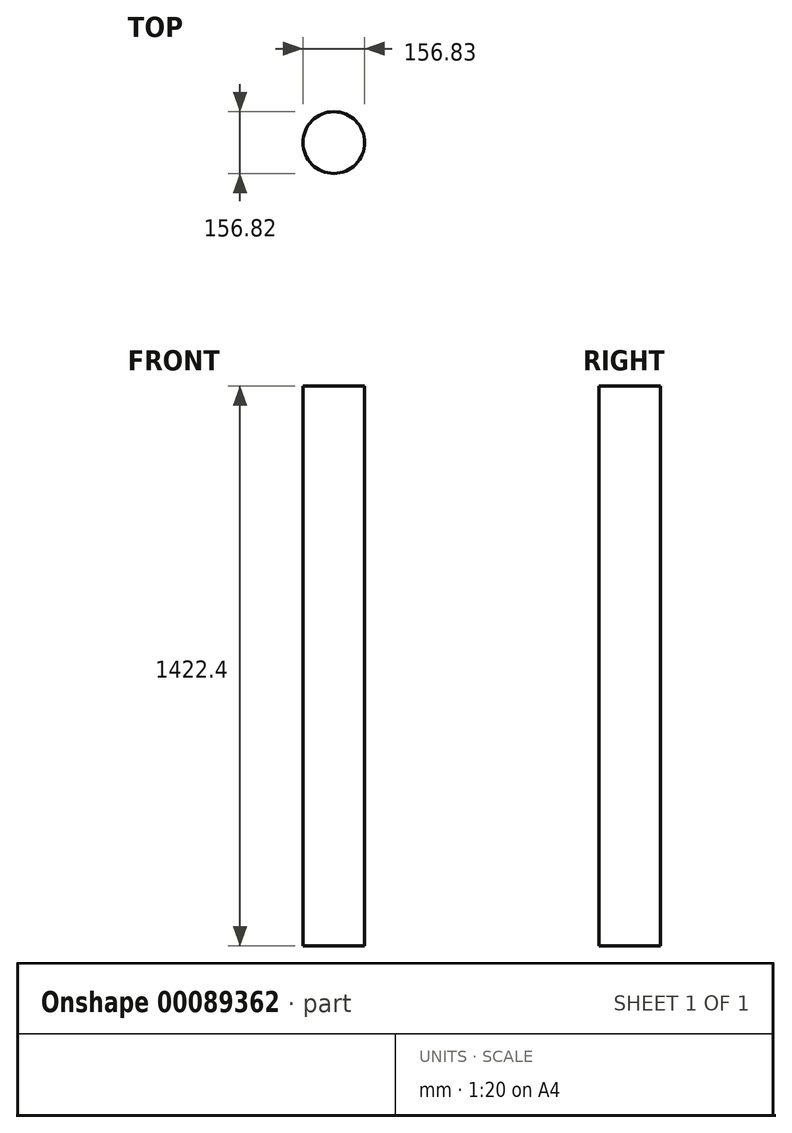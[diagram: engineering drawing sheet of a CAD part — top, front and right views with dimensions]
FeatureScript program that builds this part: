
annotation { "Feature Type Name" : "Feature", "Feature Type Description" : "" }
export const myFeature = defineFeature(function(context is Context, id is Id, definition is map)
    precondition{}
    {
        {
            var Q0;
            Q0=qCreatedBy(makeId("Top.planeOp"),FACE);
            var sketch = newSketch(context, id + "F0", { "sketchPlane" : qUnion([Q0])});
            skCircle(sketch, "E0", {"center": v(-119.78, 6.96) * mm, "radius": 78.41 * mm});
            skSolve(sketch);
        }
        {
            var Q0;
            Q0 = qSketchRegion(id + "F0", true);
            extrude(context, id + "F1", {"entities" : qUnion([Q0]), "depth" : 1422.4 * mm});
        }
    });
